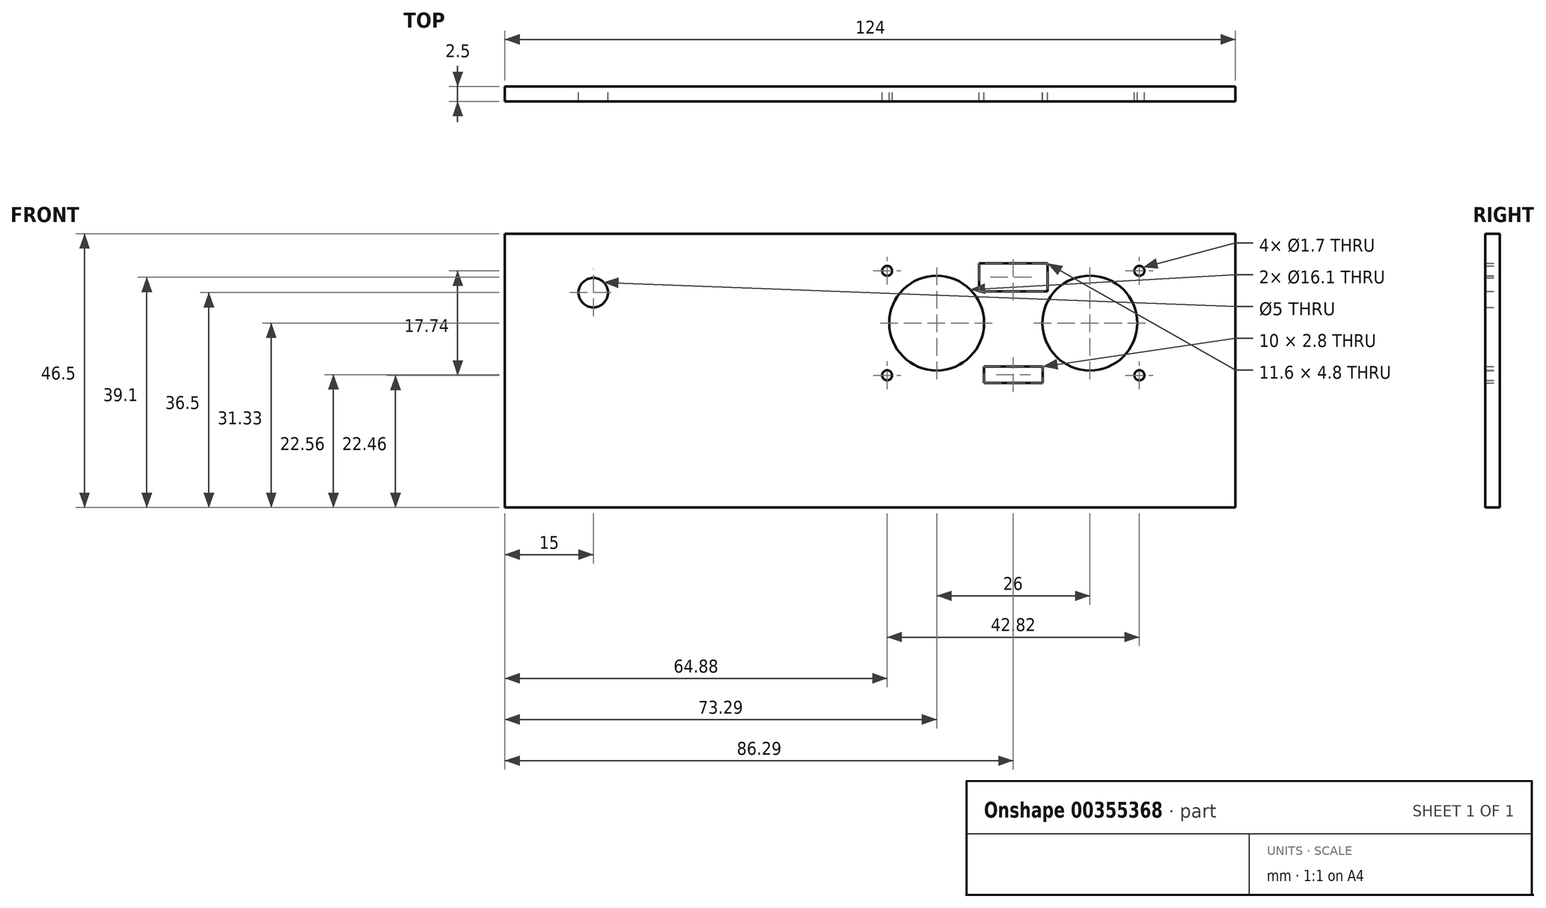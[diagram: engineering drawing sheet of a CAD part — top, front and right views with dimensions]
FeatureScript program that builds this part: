
annotation { "Feature Type Name" : "Feature", "Feature Type Description" : "" }
export const myFeature = defineFeature(function(context is Context, id is Id, definition is map)
    precondition{}
    {
        {
            var Q0;
            Q0=qCreatedBy(makeId("Front.planeOp"),FACE);
            var sketch = newSketch(context, id + "F0", { "sketchPlane" : qUnion([Q0])});
            skLineSegment(sketch, "E0.bottom", {"start": v(0, 0) * mm, "end": v(130, 0) * mm, "construction": true});
            skLineSegment(sketch, "E0.top", {"start": v(0, 52.5) * mm, "end": v(130, 52.5) * mm, "construction": true});
            skLineSegment(sketch, "E0.left", {"start": v(0, 0) * mm, "end": v(0, 52.5) * mm, "construction": true});
            skLineSegment(sketch, "E0.right", {"start": v(130, 0) * mm, "end": v(130, 52.5) * mm, "construction": true});
            skCircle(sketch, "E1", {"center": v(18, 39.5) * mm, "radius": 2.5 * mm});
            skLineSegment(sketch, "E2.0", {"start": v(3, 3) * mm, "end": v(3, 49.5) * mm});
            skLineSegment(sketch, "E2.1", {"start": v(3, 3) * mm, "end": v(127, 3) * mm});
            skLineSegment(sketch, "E2.2", {"start": v(127, 3) * mm, "end": v(127, 49.5) * mm});
            skLineSegment(sketch, "E2.3", {"start": v(3, 49.5) * mm, "end": v(127, 49.5) * mm});
            skLineSegment(sketch, "E3.bottom", {"start": v(112, 44.5) * mm, "end": v(66.58, 44.5) * mm, "construction": true});
            skLineSegment(sketch, "E3.top", {"start": v(112, 24.16) * mm, "end": v(66.58, 24.16) * mm, "construction": true});
            skLineSegment(sketch, "E3.left", {"start": v(112, 44.5) * mm, "end": v(112, 24.16) * mm, "construction": true});
            skLineSegment(sketch, "E3.right", {"start": v(66.58, 44.5) * mm, "end": v(66.58, 24.16) * mm, "construction": true});
            skLineSegment(sketch, "E4", {"start": v(89.29, 44.5) * mm, "end": v(89.29, 24.16) * mm, "construction": true});
            skLineSegment(sketch, "E5", {"start": v(66.58, 34.33) * mm, "end": v(112, 34.33) * mm, "construction": true});
            skCircle(sketch, "E6", {"center": v(102.29, 34.33) * mm, "radius": 8.05 * mm});
            skLineSegment(sketch, "E7", {"start": v(83.49, 44.5) * mm, "end": v(89.29, 44.5) * mm});
            skLineSegment(sketch, "E8", {"start": v(83.49, 44.5) * mm, "end": v(83.49, 39.7) * mm});
            skLineSegment(sketch, "E9", {"start": v(89.29, 39.7) * mm, "end": v(83.49, 39.7) * mm});
            skLineSegment(sketch, "E10", {"start": v(84.29, 26.96) * mm, "end": v(89.29, 26.96) * mm});
            skLineSegment(sketch, "E11", {"start": v(84.29, 26.96) * mm, "end": v(84.29, 24.16) * mm});
            skLineSegment(sketch, "E12", {"start": v(89.29, 24.16) * mm, "end": v(84.29, 24.16) * mm});
            skLineSegment(sketch, "E13.MirrorCS", {"start": v(89.29, 39.7) * mm, "end": v(95.09, 39.7) * mm});
            skLineSegment(sketch, "E14.MirrorCS", {"start": v(95.09, 44.5) * mm, "end": v(95.09, 39.7) * mm});
            skCircle(sketch, "E15.MirrorC", {"center": v(76.29, 34.33) * mm, "radius": 8.05 * mm});
            skLineSegment(sketch, "E16.MirrorCS", {"start": v(94.29, 26.96) * mm, "end": v(89.29, 26.96) * mm});
            skLineSegment(sketch, "E17.MirrorCS", {"start": v(94.29, 26.96) * mm, "end": v(94.29, 24.16) * mm});
            skLineSegment(sketch, "E18.MirrorCS", {"start": v(66.58, 24.16) * mm, "end": v(112, 24.16) * mm, "construction": true});
            skLineSegment(sketch, "E19", {"start": v(95.09, 44.5) * mm, "end": v(89.29, 44.5) * mm});
            skLineSegment(sketch, "E20", {"start": v(94.29, 24.16) * mm, "end": v(89.29, 24.16) * mm});
            skCircle(sketch, "E21", {"center": v(110.7, 43.2) * mm, "radius": 0.85 * mm});
            skCircle(sketch, "E22.MirrorC", {"center": v(110.7, 25.46) * mm, "radius": 0.85 * mm});
            skCircle(sketch, "E23.MirrorC", {"center": v(67.88, 43.2) * mm, "radius": 0.85 * mm});
            skCircle(sketch, "E24.MirrorC", {"center": v(67.88, 25.46) * mm, "radius": 0.85 * mm});
            skSolve(sketch);
        }
        {
            var Q0;
            Q0=qSketchRegion(id+"F0",true);
            extrude(context, id + "F1", {"entities" : qUnion([Q0]), "depth" : 2.5 * mm});
        }
    });
